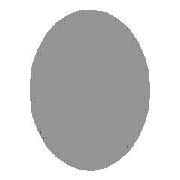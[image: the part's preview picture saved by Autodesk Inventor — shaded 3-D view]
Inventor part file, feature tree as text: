
AUTODESK INVENTOR PART (.ipt)
format: ipt  version: 2013 (Build 170138000, 138)  size: 105,984 bytes
history: native  units: mm (DEFAULTED — no unit token found)
features: other x4, sketch x3, plane x1
ambient origin geometry x8: Origin, YZ Plane, XZ Plane, XY Plane, X Axis, Y Axis, Z Axis, Center Point
bodies: Solid1 (feature_tree), Body (feature_tree)
feature tree (8):
  parser-record x1  (decoder bookkeeping rows leaked as tree rows — omitted from the tree; the rows remain in map.json)
  other  "Driven Length"
  other  "Start plane"
  other  "End plane"
  sketch  "Sketch"  dims[d2=0.0mm d4=-0.0mm d5=676.402mm d6=90.0deg d7=676.402mm]
  sketch  "Sketch2"  dims[d0=38.1mm]
  plane  "Work Plane3"
  sketch  "Sketch3"  dims[d1=676.402mm]
